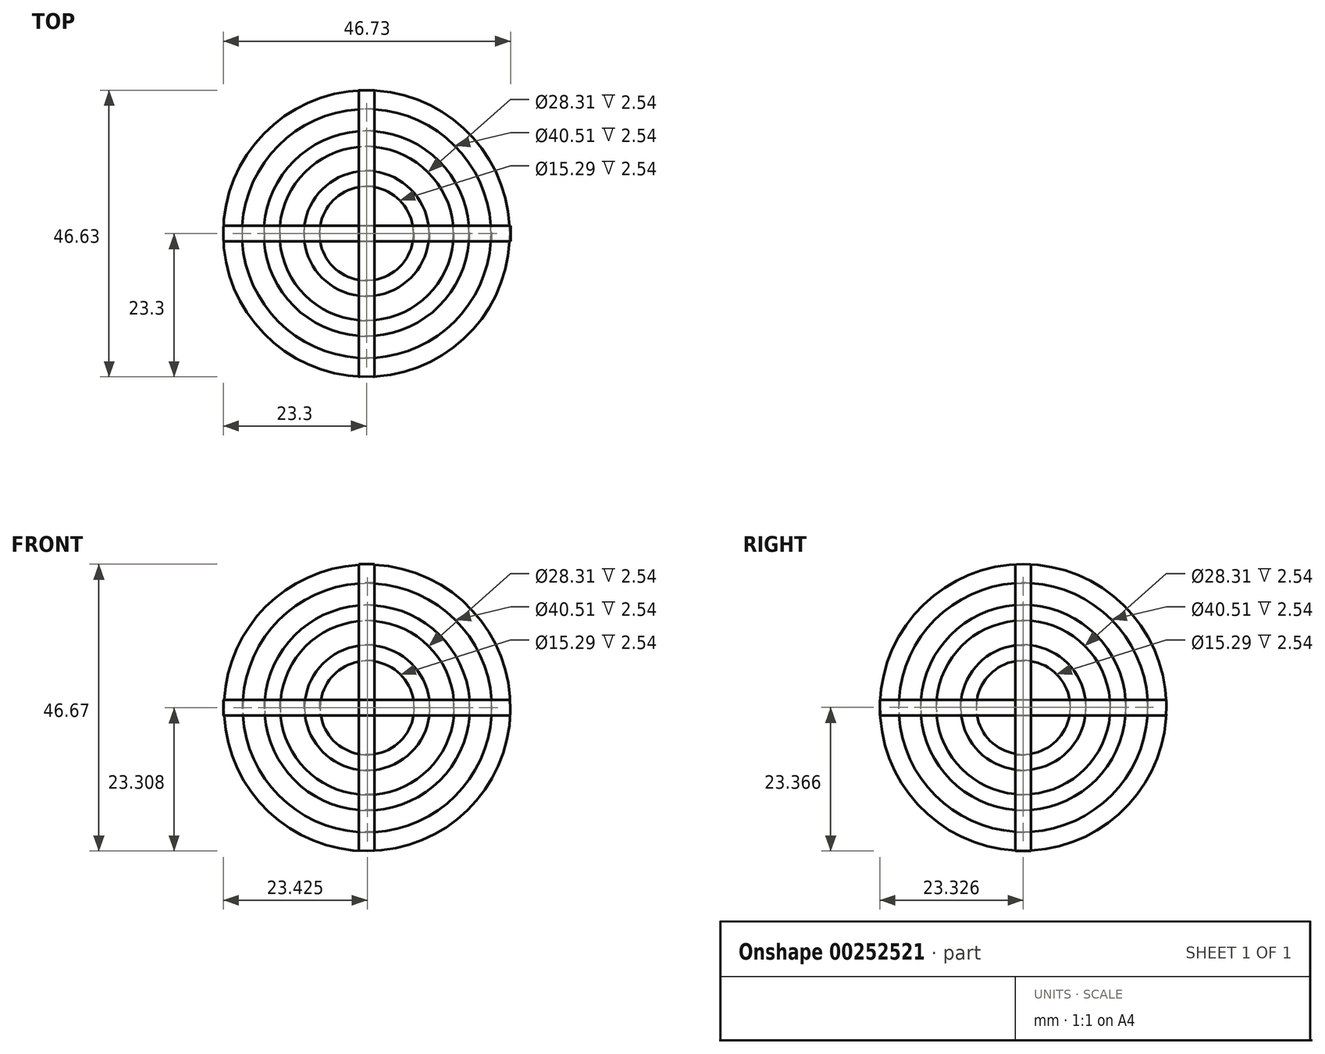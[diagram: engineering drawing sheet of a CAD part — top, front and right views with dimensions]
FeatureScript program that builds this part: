
annotation { "Feature Type Name" : "Feature", "Feature Type Description" : "" }
export const myFeature = defineFeature(function(context is Context, id is Id, definition is map)
    precondition{}
    {
        {
            var Q0;
            Q0=qCreatedBy(makeId("Top.planeOp"),FACE);
            var sketch = newSketch(context, id + "F0", { "sketchPlane" : qUnion([Q0])});
            skCircle(sketch, "E0", {"center": v(0, 0) * mm, "radius": 16.7 * mm});
            skCircle(sketch, "E1.0", {"center": v(0, 0) * mm, "radius": 14.15 * mm});
            skCircle(sketch, "E2", {"center": v(0, 0) * mm, "radius": 20.26 * mm});
            skCircle(sketch, "E3.0", {"center": v(0, 0) * mm, "radius": 23.3 * mm});
            skCircle(sketch, "E4", {"center": v(0, 0) * mm, "radius": 10.19 * mm});
            skCircle(sketch, "E5.0", {"center": v(0, 0) * mm, "radius": 7.65 * mm});
            skSolve(sketch);
        }
        {
            var Q0;
            Q0=qCreatedBy(makeId("Front.planeOp"),FACE);
            var sketch = newSketch(context, id + "F1", { "sketchPlane" : qUnion([Q0])});
            skPoint(sketch, "E6.top.end.orphan", {"position": v(-0.1, -34.25) * mm});
            skPoint(sketch, "E6.top.start.orphan", {"position": v(0.1, -34.25) * mm});
            skCircle(sketch, "E7", {"center": v(0.13, -0.03) * mm, "radius": 16.7 * mm});
            skCircle(sketch, "E8.0", {"center": v(0.13, -0.03) * mm, "radius": 14.15 * mm});
            skCircle(sketch, "E9", {"center": v(0.13, -0.03) * mm, "radius": 20.26 * mm});
            skCircle(sketch, "E10.0", {"center": v(0.13, -0.03) * mm, "radius": 23.3 * mm});
            skCircle(sketch, "E11", {"center": v(0.13, -0.03) * mm, "radius": 10.19 * mm});
            skCircle(sketch, "E12.0", {"center": v(0.13, -0.03) * mm, "radius": 7.65 * mm});
            skSolve(sketch);
        }
        {
            var Q0;
            Q0=qCreatedBy(makeId("Right.planeOp"),FACE);
            var sketch = newSketch(context, id + "F2", { "sketchPlane" : qUnion([Q0])});
            skCircle(sketch, "E13", {"center": v(0.03, 0.03) * mm, "radius": 16.7 * mm});
            skCircle(sketch, "E14.0", {"center": v(0.03, 0.03) * mm, "radius": 14.15 * mm});
            skCircle(sketch, "E15", {"center": v(0.03, 0.03) * mm, "radius": 20.26 * mm});
            skCircle(sketch, "E16.0", {"center": v(0.03, 0.03) * mm, "radius": 23.3 * mm});
            skCircle(sketch, "E17", {"center": v(0.03, 0.03) * mm, "radius": 10.19 * mm});
            skCircle(sketch, "E18.0", {"center": v(0.03, 0.03) * mm, "radius": 7.65 * mm});
            skSolve(sketch);
        }
        {
            var Q0;
            Q0=makeQuery(id+"F0.imprint","IMPRINT",FACE,{"disambiguationData":[TD([[makeQuery(id+"F0.imprint","IMPRINT",EDGE,{"derivedFrom":sQuery(id+"F0.wireOp",EDGE,"E0")}),1.0]])]});
            var Q1;
            Q1=makeQuery(id+"F0.imprint","IMPRINT",FACE,{"disambiguationData":[TD([[makeQuery(id+"F0.imprint","IMPRINT",EDGE,{"derivedFrom":sQuery(id+"F0.wireOp",EDGE,"E2")}),-1.0]])]});
            var Q2;
            Q2=makeQuery(id+"F0.imprint","IMPRINT",FACE,{"disambiguationData":[TD([[makeQuery(id+"F0.imprint","IMPRINT",EDGE,{"derivedFrom":sQuery(id+"F0.wireOp",EDGE,"E4")}),1.0]])]});
            extrude(context, id + "F3", {"entities" : qUnion([Q0, Q1, Q2]), "endBound" : BoundingType.SYMMETRIC, "depth" : 2.54 * mm, "offsetDistance" : 25.4 * mm});
        }
        {
            var Q0;
            Q0=makeQuery(id+"F1.imprint","IMPRINT",FACE,{"disambiguationData":[TD([[makeQuery(id+"F1.imprint","IMPRINT",EDGE,{"derivedFrom":sQuery(id+"F1.wireOp",EDGE,"E9")}),-1.0]])]});
            var Q1;
            Q1=makeQuery(id+"F1.imprint","IMPRINT",FACE,{"disambiguationData":[TD([[makeQuery(id+"F1.imprint","IMPRINT",EDGE,{"derivedFrom":sQuery(id+"F1.wireOp",EDGE,"E7")}),1.0]])]});
            var Q2;
            Q2=makeQuery(id+"F1.imprint","IMPRINT",FACE,{"disambiguationData":[TD([[makeQuery(id+"F1.imprint","IMPRINT",EDGE,{"derivedFrom":sQuery(id+"F1.wireOp",EDGE,"E11")}),1.0]])]});
            extrude(context, id + "F4", {"entities" : qUnion([Q0, Q1, Q2]), "endBound" : BoundingType.SYMMETRIC, "depth" : 2.54 * mm, "offsetDistance" : 25.4 * mm});
        }
        {
            var Q0;
            Q0=makeQuery(id+"F2.imprint","IMPRINT",FACE,{"disambiguationData":[TD([[makeQuery(id+"F2.imprint","IMPRINT",EDGE,{"derivedFrom":sQuery(id+"F2.wireOp",EDGE,"E15")}),-1.0]])]});
            var Q1;
            Q1=makeQuery(id+"F2.imprint","IMPRINT",FACE,{"disambiguationData":[TD([[makeQuery(id+"F2.imprint","IMPRINT",EDGE,{"derivedFrom":sQuery(id+"F2.wireOp",EDGE,"E13")}),1.0]])]});
            var Q2;
            Q2=makeQuery(id+"F2.imprint","IMPRINT",FACE,{"disambiguationData":[TD([[makeQuery(id+"F2.imprint","IMPRINT",EDGE,{"derivedFrom":sQuery(id+"F2.wireOp",EDGE,"E17")}),1.0]])]});
            extrude(context, id + "F5", {"entities" : qUnion([Q0, Q1, Q2]), "endBound" : BoundingType.SYMMETRIC, "depth" : 2.54 * mm, "offsetDistance" : 25.4 * mm});
        }
    });
